# Revit family: Pump_Heavy_Duty-Solid_Handling-Zoeller-61_HD_Vertical_Series
name_source: partatom
category: Mechanical Equipment
units: mm (PartAtom-declared; Revit-internal decimal feet)

## family parameters
Always vertical = No
Cut with Voids When Loaded = No
OmniClass Number = 23.60.30.21
OmniClass Title = Pumps
Part Type = Normal
Room Calculation Point = No
Round Connector Dimension = Use Radius
Shared = Yes
Work Plane-Based = Yes

## types (9) — shared parameters
Assembly Code = D2010900
Default Elevation = 0"
Description = Commercial Effluent Pumps
Discharge Diameter = 3"
Discharge Radius = 1 1/2"
Finish = Cast Iron-Zoeller-Powder Coated Epoxy
Flange = ANSI B16.1
Height = 29 1/4"
Hertz = 60
Impeller Type (Optional) = Ductile Iron Vortex
Installation Type = Floor Mounted
Insulation = Class F
Lead Wires Insulation = Class F
Length = 17 9/16"
Manufacturer = Zoeller
Material = Cast Iron-Zoeller-Powder Coated Epoxy
Max. Stator Temp. = 311 °F
Max. Water Temp. = 104 °F
Mechanical Seals = Tandem carbon/ceramic upper and silicon carbide/silicon carbide lower
Min. Recommended Fluid Level = 24"
Moisture Sensor (Optional) = Moisture Sensing Probes (Requires a circuit in control panel)
Motor Design Letter = NEMA B
Motor Shaft = 416 S.S.
Motor Thermal Shutoff (Single Phase Only) = Thermal Sensors With Automatic Reset
O-Rings and Cover Gasket = Buna-N
Operation = Non-Automatic
Phase = 1 or 3
Power Cord = #12-4 SO (Models with a FLA greater than 20 amps use #8-4 gauge power cord)
Price = Prices may vary. Please consult Manufacturer Representative for most up-to-date price list.
Product Page URL = https://www.zoellerengineered.com
Revised Date = 03/06/2023
Shaft Seal Lower (Options) = Carbon/Silicon Carbide, Silicon Carbide/Silicon Carbide
Shaft Seal Lower Standard = Silicon Carbide/Carbon
Shaft Seal Upper (Options) = Silicon Carbide/Carbon, Silicon Carbide/Silicon Carbide
Shaft Seal Upper Standard = Carbon/Ceramic
Shipping Weight = 245 lbs (111 kg)
Solid Size = 2 1/2" (64 mm)
Tandem Seals = Standard
Type = Permanent Split Capacitor or 3 Phase
Type SOW Power Cord Length = 300"
URL = https://www.zoellerengineered.com
Warranty Information = 36 Months (Limited)
Waste Connection = Yes
Width = 12 5/8"

## per-type parameters (varying)
| type | Dry Pit (1-3 BHP, Intermittent Duty) | Full Load Amps (Voltage Dependent) | High Temp (1-3 BHP Only) | Impeller Diameter | Impeller Type | Inverter Duty Submersible (1-5 BHP Only) | Locked Rotor Amps (Voltage Dependant) | Maximum KW Input | Motor | Motor Type | NEC Locked Rotor Code | Product Documentation Link | RPM | Service Factor | Voltage |
| 6121-3" | Yes | 2.0 - 8.9 | Yes | 5 3/8" | Ductile Iron Semi-Open | Yes | 11.5 - 48.0 | 1.9 | 1.5 BHP | Standard Submersible | J | https://www.zoellerengineered.com | 1750 | 1.2 | 200 / 230 / 460 / 575 |
| 6120-3" | Yes | 1.6 - 6.9 | Yes | 4 7/8" | Ductile Iron Semi-Open | Yes | 11.5 - 48.0 | 1.4 | 1.0 BHP | Standard Submersible | M | https://www.zoellerengineered.com | 1750 | 1.2 | 200 / 230 / 460 / 575 |
| 6122-3" | Yes | 2.7 - 14.5 | Yes | 5 3/4" | Ductile Iron Semi-Open | Yes | 16.5 - 86.0 | 2.4 | 2.0 BHP | Standard Submersible | K | https://www.zoellerengineered.com | 1750 | 1.2 | 200 / 230 / 460 / 575 |
| 6123-3" | Yes | 3.9 - 17.0 | Yes | 6 3/8" | Ductile Iron Semi-Open | Yes | 16.2 - 86.0 | 3.5 | 3.0 BHP | Standard Submersible | F |  | 1750 | 1.2 | 200 / 230 / 460 / 575 |
| 6124-3" | No | 6.1 - 28.0 | No | 7" | Ductile Iron Semi-Open | Yes | 23.0 - 139.0 | 5.5 | 5.0 BHP | Standard Submersible | E | https://www.zoellerengineered.com | 1750 | 1.2 | 200 / 230 / 460 / 575 |
| 6125-3" | No | 9.0 - 25.3 | No | 7 1/2" | Ductile Iron Semi-Open | No | 29.0 - 83.0 | 6.9 | 7.5 BHP | Standard Submersible | C | https://www.zoellerengineered.com | 1750 | 1.0 | 200 / 230 / 460 / 575 |
| 6111-3" | No | 6.1 - 28.0 | No | 4 3/8" | Bronze Semi-Open | Yes | 25.2 - 132.0 | 5.3 | 5.0 BHP | Submersible | E | https://www.zoellerengineered.com | 3450 | 1.2 | 200 / 230 / 460 / 575 |
| 6112-3" | No | 9.0 - 25.3 | No | 4 3/4" | Bronze Semi-Open | No | 36.0 - 94.0 | 7.8 | 7.5 BHP | Submersible | D | https://www.zoellerengineered.com | 3450 | 1.2 | 200 / 230 / 460 |
| 6113-3" | No | 11.0 - 32.2 | No | 5 1/8" | Bronze Semi-Open | No | 36.0 - 94.0 | 10.5 | 10.0 BHP | Submersible | B | https://www.zoellerengineered.com | 3450 | 1.0 | 200 / 230 / 460 |

note: column(s) folded — value = type name in every type: Model

## geometry (parser evidence)
native form markers: Sweep x3
no freeform markers — native parametric forms only
